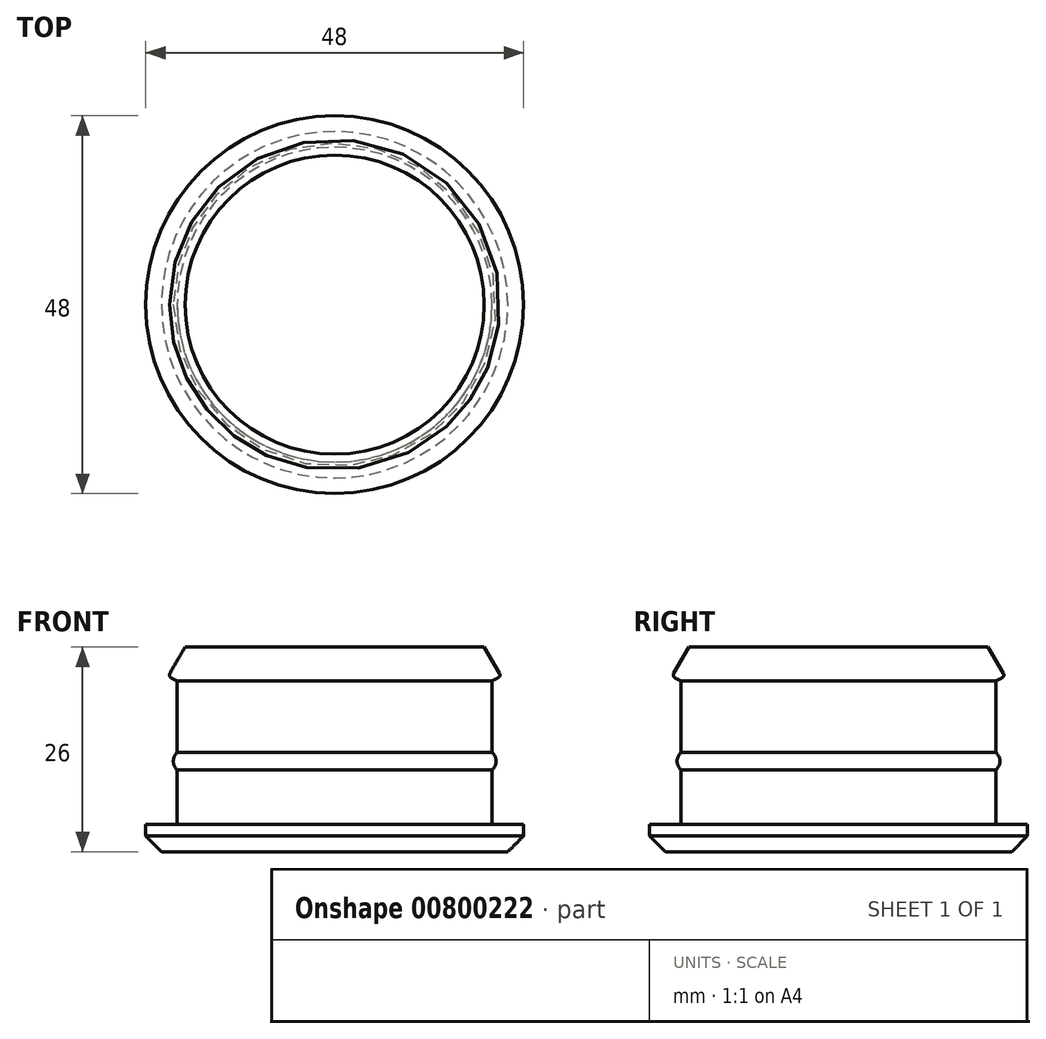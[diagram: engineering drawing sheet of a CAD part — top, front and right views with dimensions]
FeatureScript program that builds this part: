
annotation { "Feature Type Name" : "Feature", "Feature Type Description" : "" }
export const myFeature = defineFeature(function(context is Context, id is Id, definition is map)
    precondition{}
    {
        {
            var Q0;
            Q0=qCreatedBy(makeId("Front.planeOp"),FACE);
            var sketch = newSketch(context, id + "F0", { "sketchPlane" : qUnion([Q0])});
            skLineSegment(sketch, "E0", {"start": v(0, 0) * mm, "end": v(0, 26) * mm});
            skLineSegment(sketch, "E1", {"start": v(0, 26) * mm, "end": v(19, 26) * mm});
            skLineSegment(sketch, "E2", {"start": v(19, 26) * mm, "end": v(21.5, 21.7) * mm});
            skLineSegment(sketch, "E3", {"start": v(21.5, 21.7) * mm, "end": v(20, 21.7) * mm});
            skLineSegment(sketch, "E4", {"start": v(20, 21.7) * mm, "end": v(20, 12.62) * mm});
            skLineSegment(sketch, "E5", {"start": v(20, 3.5) * mm, "end": v(24, 3.5) * mm});
            skLineSegment(sketch, "E6", {"start": v(24, 3.5) * mm, "end": v(24, 0) * mm});
            skLineSegment(sketch, "E7", {"start": v(24, 0) * mm, "end": v(0, 0) * mm});
            skArc(sketch, "E8", {"start": v(20, 10.38) * mm, "mid": v(20.5, 11.5) * mm, "end": v(20, 12.62) * mm});
            skLineSegment(sketch, "E9.trimOffspring", {"start": v(20, 10.38) * mm, "end": v(20, 3.5) * mm});
            skSolve(sketch);
        }
        {
            var Q0;
            Q0=makeQuery(id+"F0.imprint","IMPRINT",FACE,{"disambiguationData":[TD([[makeQuery(id+"F0.imprint","IMPRINT",EDGE,{"derivedFrom":sQuery(id+"F0.wireOp",EDGE,"E0")}),-1.0]])]});
            var Q1;
            Q1=sQuery(id+"F0.wireOp",EDGE,"E0");
            revolve(context, id + "F1", {"surfaceOperationType" : NewSurfaceOperationType.NEW, "entities" : qUnion([Q0]), "axis" : qUnion([Q1]), "revolveType" : RevolveType.FULL});
        }
        {
            var Q0;
            Q0=makeQuery(id+"F1.opRevolve","SWEPT_EDGE",EDGE,{"disambiguationData":[OSD([sQuery(id+"F0.wireOp",EDGE,"E6"),sQuery(id+"F0.wireOp",EDGE,"E7")])]});
            chamfer(context, id + "F2", {"entities" : qUnion([Q0]), "width" : 2 * mm, "tangentPropagation" : true});
        }
        {
            var Q0;
            Q0=makeQuery(id+"F1.opRevolve","SWEPT_EDGE",EDGE,{"disambiguationData":[OSD([sQuery(id+"F0.wireOp",EDGE,"E2"),sQuery(id+"F0.wireOp",EDGE,"E3")])]});
            chamfer(context, id + "F3", {"entities" : qUnion([Q0]), "chamferType" : ChamferType.TWO_OFFSETS, "width1" : 1.5 * mm, "oppositeDirection" : false, "width2" : 0.7 * mm, "tangentPropagation" : true});
        }
        {
            var Q0;
            {var subQ0=sQuery(id+"F0.wireOp",EDGE,"E2");Q0=makeQuery(id+"F3.opChamfer","BLEND_EDGE",EDGE,{"blendedFrom":[makeQuery(id+"F1.opRevolve","SWEPT_EDGE",EDGE,{"disambiguationData":[OSD([subQ0,sQuery(id+"F0.wireOp",EDGE,"E3")])]}),makeQuery(id+"F1.opRevolve","SWEPT_FACE",FACE,{"disambiguationData":[OSD([subQ0])]})],"blendedInto":[makeQuery(id+"F1.opRevolve","SWEPT_FACE",FACE,{"disambiguationData":[OSD([subQ0])]})]});}
            fillet(context, id + "F4", {"entities" : qUnion([Q0]), "radius" : 0.4 * mm, "tangentPropagation" : true, "allowEdgeOverflow" : false});
        }
    });
